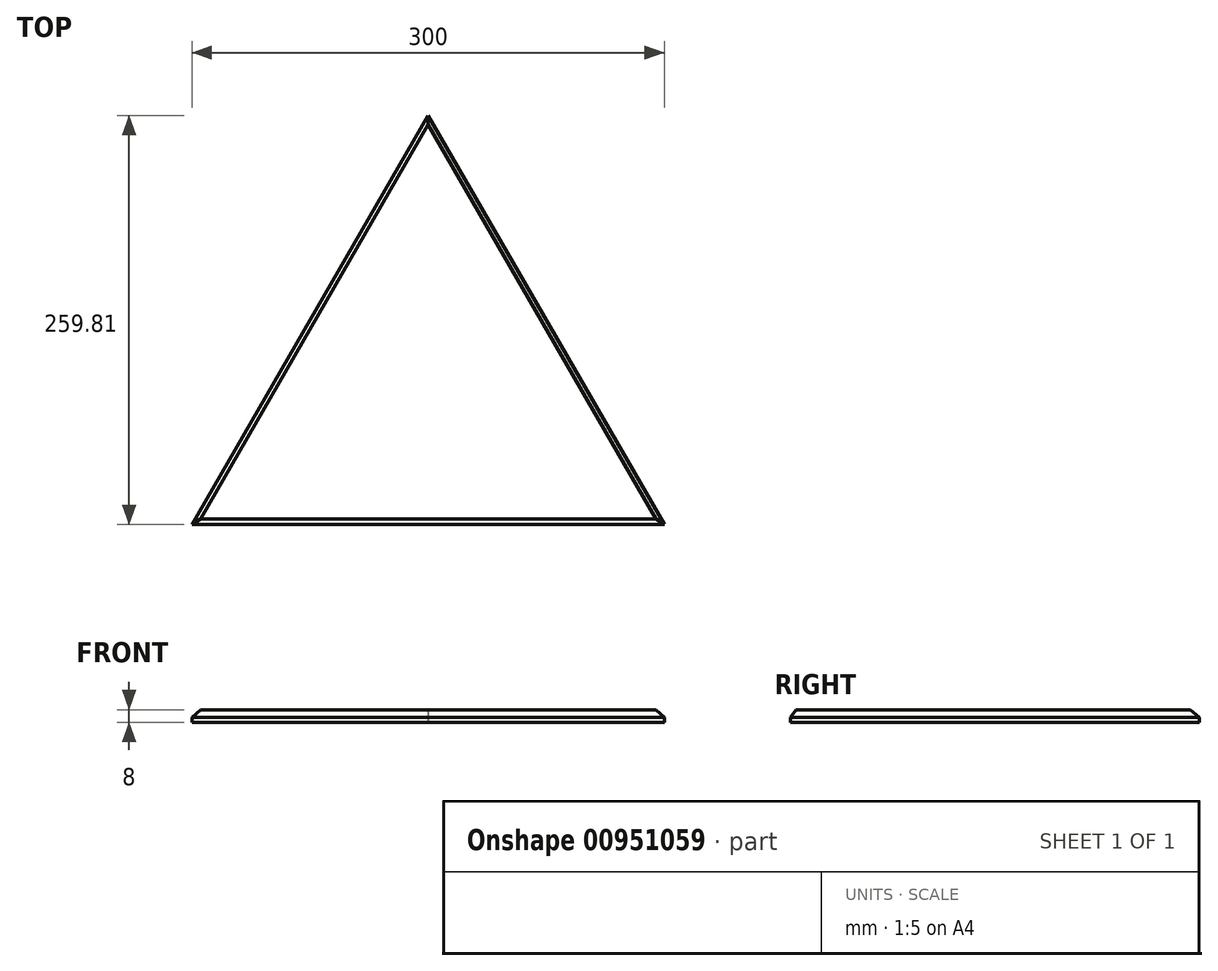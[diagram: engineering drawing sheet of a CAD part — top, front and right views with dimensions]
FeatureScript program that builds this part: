
annotation { "Feature Type Name" : "Feature", "Feature Type Description" : "" }
export const myFeature = defineFeature(function(context is Context, id is Id, definition is map)
    precondition{}
    {
        {
            var Q0;
            Q0=qCreatedBy(makeId("Top.planeOp"),FACE);
            var sketch = newSketch(context, id + "F0", { "sketchPlane" : qUnion([Q0])});
            skLineSegment(sketch, "E0", {"start": v(150, 0) * mm, "end": v(-150, 0) * mm});
            skLineSegment(sketch, "E1", {"start": v(-150, 0) * mm, "end": v(0, 259.8) * mm});
            skLineSegment(sketch, "E2", {"start": v(0, 259.8) * mm, "end": v(150, 0) * mm});
            skSolve(sketch);
        }
        {
            var Q0;
            Q0 = qSketchRegion(id + "F0", true);
            extrude(context, id + "F1", {"entities" : qUnion([Q0]), "depth" : 8 * mm, "offsetDistance" : 25 * mm});
        }
        {
            var Q0;
            Q0=makeQuery(id+"F1.opExtrude","CAP_EDGE",EDGE,{"disambiguationData":[OSD([sQuery(id+"F0.wireOp",EDGE,"E1")])],"isStart":false});
            var Q1;
            Q1=makeQuery(id+"F1.opExtrude","CAP_EDGE",EDGE,{"disambiguationData":[OSD([sQuery(id+"F0.wireOp",EDGE,"E2")])],"isStart":false});
            chamfer(context, id + "F2", {"entities" : qUnion([Q0, Q1]), "chamferType" : ChamferType.OFFSET_ANGLE, "width" : 5 * mm, "oppositeDirection" : false, "angle" : 30 * degree, "tangentPropagation" : true});
        }
        {
            var Q0;
            Q0=makeQuery(id+"F1.opExtrude","CAP_EDGE",EDGE,{"disambiguationData":[OSD([sQuery(id+"F0.wireOp",EDGE,"E0")])],"isStart":false});
            chamfer(context, id + "F3", {"entities" : qUnion([Q0]), "chamferType" : ChamferType.OFFSET_ANGLE, "width" : 5 * mm, "oppositeDirection" : false, "angle" : 35 * degree, "tangentPropagation" : true});
        }
    });
